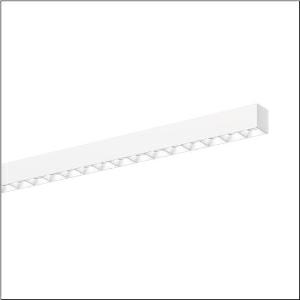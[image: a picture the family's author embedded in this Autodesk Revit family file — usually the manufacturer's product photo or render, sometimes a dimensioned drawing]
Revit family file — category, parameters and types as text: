
# Revit family: silica_r__21_51mx26dc4awb_5f84
name_source: partatom
category: Lighting Fixtures
units: mm (PartAtom-declared; Revit-internal decimal feet)

## family parameters
Cut with Voids When Loaded = No
Host = Face
Light Source = No
Part Type = Normal
Room Calculation Point = No
Round Connector Dimension = Use Diameter
Shared = No

## types (1)
- --- (1 x LED, 10800 lm, 60.6 W, 4000K)
    Apparent Load = 61 VA
    CIE Flux Codes = 83 98 100 100 100
    Color Rendering = 80
    Color Temperature = 4000K
    Default Elevation = 1800 mm
    Description = Silica® 21, office luminaire, primary light control with darklight reflector, of PMMA, white, CAT 2 (L<= 3000cd/m²), light emission: direct distribution, primary light characteristic: symmetric, installation type: surface-mounted, LED, rated luminous flux: 10.800lm, luminous efficacy: 178lm/W, light colour: 840, colour temperature: 4000K, with terminal, 3+2-pole, max. 2.5mm², mains connection: 220..240V, AC, 50/60Hz, rated input power: 60.6W, luminaire housing, of aluminium, traffic white (RAL 9016), length: 3.004mm, width: 53mm, height: 53mm, protection rating (complete): IP20, insulation class (complete): insulation class I (protective earthing), certification: CE, permissible operating ambient temperature: 0..+35°C, standard: EN 50419, packaging unit: 1 piece
    Height = 0 mm  [stored 0 ft]
    Lamp = 1 x LED
    Lamp Light Flux = 10800 lm
    Lamp Power = 60.6 W
    Lamp count = 1
    Length = 3004 mm
    Luminous efficacy = 178 lm/W
    Manufacturer = Siteco
    ModVariant = No
    Model = 51MX26DC4AWB
    Mounting Place = Ceiling
    Mounting Type = Recessed
    Number of Poles = 1
    OnlyDefault = Yes
    Power Factor = 1
    Product Name = Silica® 21
    Product group = office luminaire | ceiling recessed
    ProductGroupID = 400
    Protection Class = Protection class I
    Protection Degree = IP 20
    RLX_Detail_Level = 1
    RLX_Emergency_Light_Flux = 0 lm
    RLX_Emergency_Type = 0
    RLX_Emergency_Type_DB = No
    RlxData = <blob elided: 60825 chars, md5=c3c5e8c7>
    Socket = socket
    Standby Power = 0 W
    System Light Flux = 10800 lm
    System Power = 61 W
    Type Comments = factory setting: luminous flux: 100 % | dim-lin: 254 | 336 mA
    Type Image = l_1335934.jpg
    URL = http://relux.com
    VarID = @adj_094133
    Voltage = 0 V
    Weight = 0.00 kg
    Width = 53 mm

note: [stored X ft] marks values corroborated as IEEE doubles in the binary element streams (Revit-internal decimal feet)

## geometry (parser evidence)
native form markers: Blend x4, Sweep x13
no freeform markers — native parametric forms only
